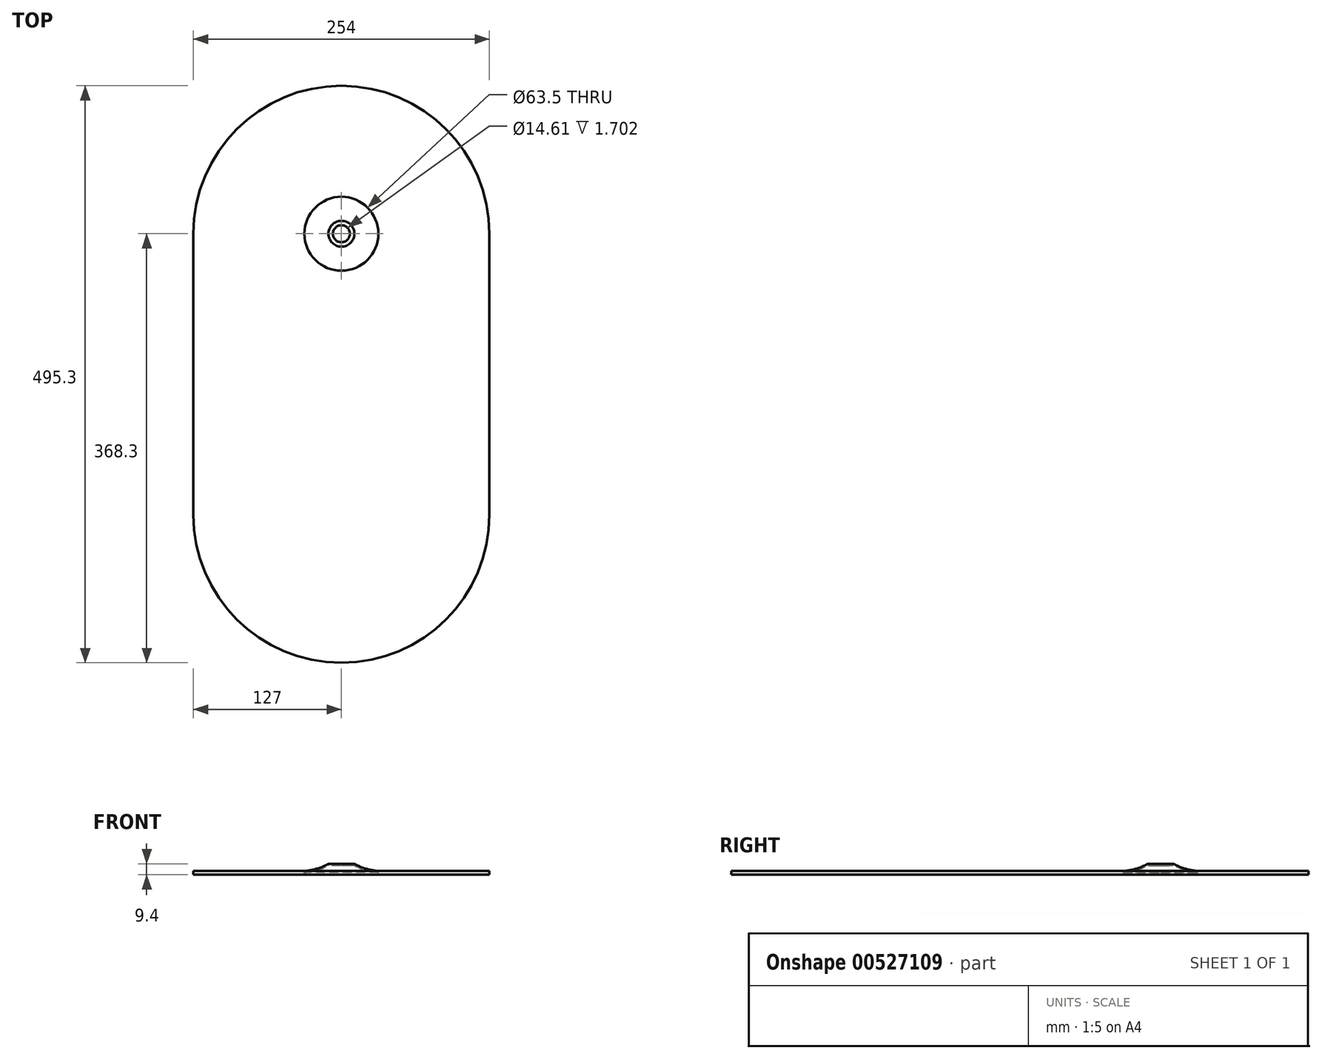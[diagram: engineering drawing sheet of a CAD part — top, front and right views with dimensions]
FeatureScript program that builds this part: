
annotation { "Feature Type Name" : "Feature", "Feature Type Description" : "" }
export const myFeature = defineFeature(function(context is Context, id is Id, definition is map)
    precondition{}
    {
        {
            var Q0;
            Q0=qCreatedBy(makeId("Top.planeOp"),FACE);
            var sketch = newSketch(context, id + "F0", { "sketchPlane" : qUnion([Q0])});
            skCircle(sketch, "E0", {"center": v(0, 120.65) * mm, "radius": 101.6 * mm});
            skLineSegment(sketch, "E1", {"start": v(0, 120.65) * mm, "end": v(0, -120.65) * mm, "construction": true});
            skPoint(sketch, "E2", {"position": v(0, 0) * mm});
            skCircle(sketch, "E3", {"center": v(0, -120.65) * mm, "radius": 101.6 * mm});
            skSolve(sketch);
        }
        {
            var Q0;
            Q0=qCreatedBy(makeId("Top.planeOp"),FACE);
            var sketch = newSketch(context, id + "F1", { "sketchPlane" : qUnion([Q0])});
            skLineSegment(sketch, "E4.bottom", {"start": v(127, 120.65) * mm, "end": v(-127, 120.65) * mm, "construction": true});
            skLineSegment(sketch, "E4.top", {"start": v(127, -120.65) * mm, "end": v(-127, -120.65) * mm, "construction": true});
            skLineSegment(sketch, "E4.left", {"start": v(127, 120.65) * mm, "end": v(127, -120.65) * mm});
            skLineSegment(sketch, "E4.right", {"start": v(-127, 120.65) * mm, "end": v(-127, -120.65) * mm});
            skPoint(sketch, "E4.middle", {"position": v(0, 0) * mm});
            skArc(sketch, "E5", {"start": v(127, 120.65) * mm, "mid": v(0, 247.65) * mm, "end": v(-127, 120.65) * mm});
            skArc(sketch, "E6", {"start": v(-127, -120.65) * mm, "mid": v(0, -247.65) * mm, "end": v(127, -120.65) * mm});
            skCircle(sketch, "E7", {"center": v(0, 120.65) * mm, "radius": 31.75 * mm});
            skCircle(sketch, "E8", {"center": v(0, -120.65) * mm, "radius": 31.75 * mm});
            skSolve(sketch);
        }
        {
            var Q0;
            Q0=qCreatedBy(makeId("Right.planeOp"),FACE);
            var sketch = newSketch(context, id + "F2", { "sketchPlane" : qUnion([Q0])});
            skPoint(sketch, "E9.0", {"position": v(120.65, 0) * mm});
            skLineSegment(sketch, "E10.0", {"start": v(88.9, 0) * mm, "end": v(152.4, 0) * mm, "construction": true});
            skLineSegment(sketch, "E11.0", {"start": v(-152.4, 0) * mm, "end": v(-88.9, 0) * mm, "construction": true});
            skPoint(sketch, "E12.0", {"position": v(-120.65, 0) * mm});
            skLineSegment(sketch, "E13", {"start": v(131.76, 6.22) * mm, "end": v(127.95, 6.22) * mm});
            skArc(sketch, "E14", {"start": v(131.76, 6.22) * mm, "mid": v(141.75, 2) * mm, "end": v(152.4, 0) * mm});
            skLineSegment(sketch, "E15", {"start": v(127.95, 6.22) * mm, "end": v(127.95, 4.52) * mm});
            skLineSegment(sketch, "E16", {"start": v(127.95, 4.52) * mm, "end": v(131.44, 4.52) * mm});
            skLineSegment(sketch, "E17", {"start": v(152.4, 0) * mm, "end": v(152.4, -1.3) * mm});
            skLineSegment(sketch, "E18", {"start": v(131.44, 4.52) * mm, "end": v(131.44, 4.93) * mm});
            skArc(sketch, "E19", {"start": v(131.44, 4.93) * mm, "mid": v(141.59, 0.7) * mm, "end": v(152.4, -1.3) * mm});
            skLineSegment(sketch, "E20", {"start": v(120.65, 13.5) * mm, "end": v(120.65, -16.53) * mm, "construction": true});
            skSolve(sketch);
        }
        {
            var Q0;
            Q0=makeQuery(id+"F1.imprint","IMPRINT",FACE,{"disambiguationData":[TD([[makeQuery(id+"F1.imprint","IMPRINT",EDGE,{"derivedFrom":sQuery(id+"F1.wireOp",EDGE,"E4.left")}),-1.0]])]});
            var Q1;
            Q1=makeQuery(id+"F1.imprint","IMPRINT",FACE,{"disambiguationData":[TD([[makeQuery(id+"F1.imprint","IMPRINT",EDGE,{"derivedFrom":sQuery(id+"F1.wireOp",EDGE,"E8")}),1.0]])]});
            extrude(context, id + "F3", {"entities" : qUnion([Q0, Q1]), "oppositeDirection" : true, "depth" : 3.17 * mm, "offsetDistance" : 25.4 * mm});
        }
        {
            var Q0;
            Q0 = qSketchRegion(id + "F2", true);
            var Q1;
            Q1=sQuery(id+"F2.wireOp",EDGE,"E20");
            revolve(context, id + "F4", {"operationType" : NewBodyOperationType.ADD, "entities" : qUnion([Q0]), "axis" : qUnion([Q1]), "revolveType" : RevolveType.FULL});
        }
    });
